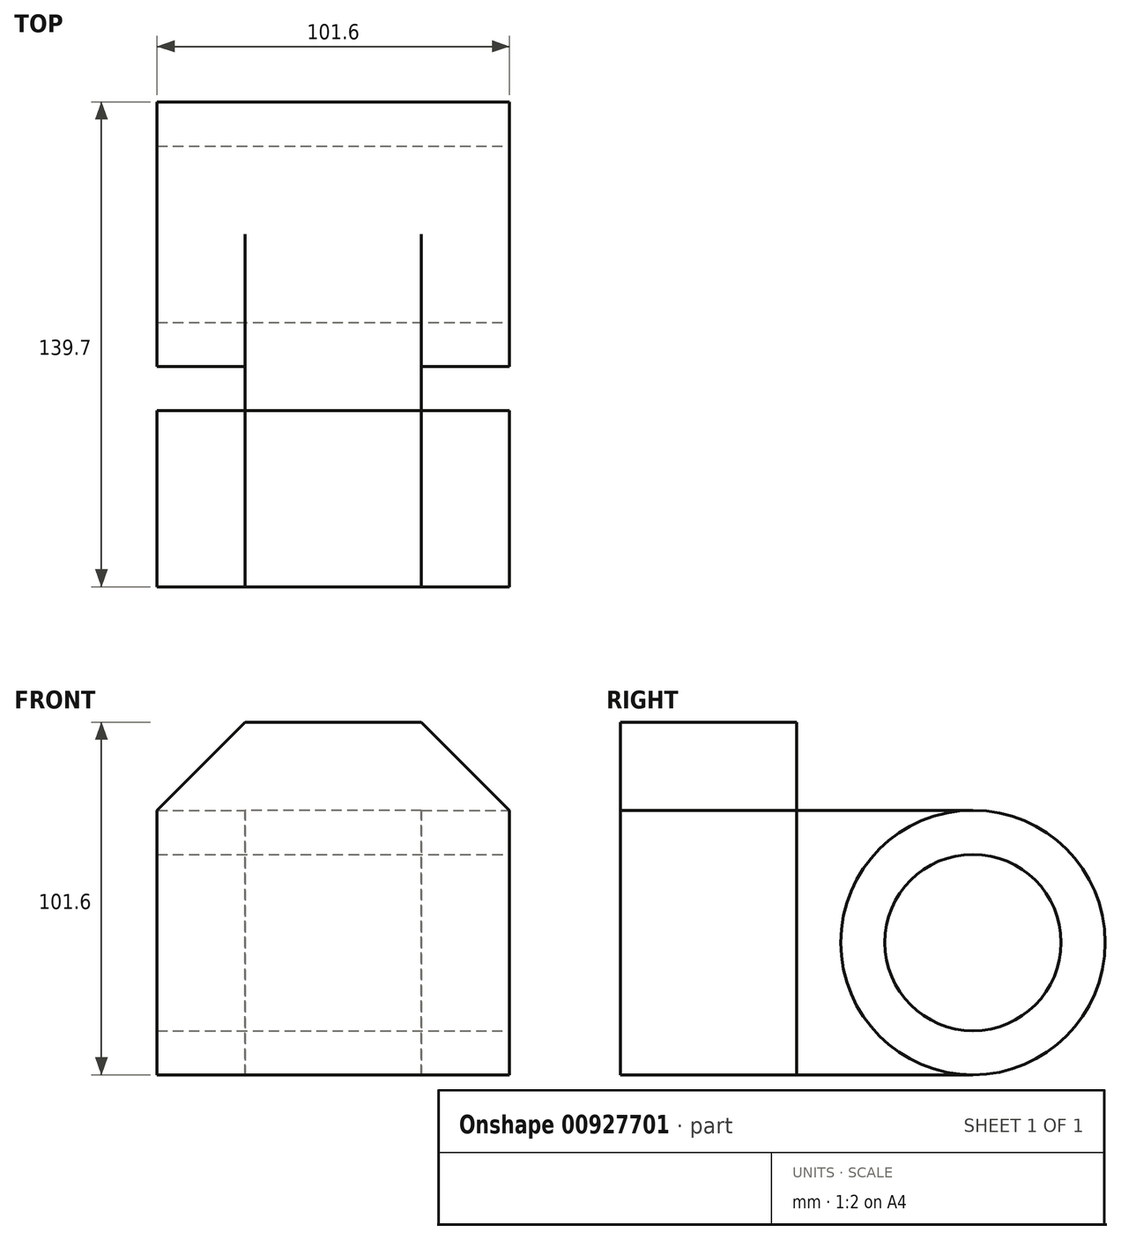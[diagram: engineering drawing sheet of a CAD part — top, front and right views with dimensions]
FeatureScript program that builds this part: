
annotation { "Feature Type Name" : "Feature", "Feature Type Description" : "" }
export const myFeature = defineFeature(function(context is Context, id is Id, definition is map)
    precondition{}
    {
        {
            var Q0;
            Q0=qCreatedBy(makeId("Top.planeOp"),FACE);
            var sketch = newSketch(context, id + "F0", { "sketchPlane" : qUnion([Q0])});
            skLineSegment(sketch, "E0.bottom", {"start": v(0, 0) * mm, "end": v(-101.6, 0) * mm});
            skLineSegment(sketch, "E0.top", {"start": v(0, 50.8) * mm, "end": v(-101.6, 50.8) * mm});
            skLineSegment(sketch, "E0.left", {"start": v(0, 0) * mm, "end": v(0, 50.8) * mm});
            skLineSegment(sketch, "E0.right", {"start": v(-101.6, 0) * mm, "end": v(-101.6, 50.8) * mm});
            skSolve(sketch);
        }
        {
            var Q0;
            Q0 = qSketchRegion(id + "F0", true);
            extrude(context, id + "F1", {"entities" : qUnion([Q0]), "depth" : 101.6 * mm, "offsetDistance" : 25.4 * mm});
        }
        {
            var Q0;
            Q0=makeQuery(id+"F1.opExtrude","SWEPT_FACE",FACE,{"disambiguationData":[OSD([sQuery(id+"F0.wireOp",EDGE,"E0.top")])]});
            var sketch = newSketch(context, id + "F2", { "sketchPlane" : qUnion([Q0])});
            skLineSegment(sketch, "E1", {"start": v(25.4, 101.6) * mm, "end": v(0, 76.2) * mm});
            skLineSegment(sketch, "E2", {"start": v(76.2, 101.6) * mm, "end": v(101.6, 76.2) * mm});
            skSolve(sketch);
        }
        {
            var Q0;
            {var subQ0=sQuery(id+"F2.wireOp",EDGE,"E1");Q0=makeQuery(id+"F2.imprint","IMPRINT",FACE,{"disambiguationData":[TD([[makeQuery(id+"F2.imprint","IMPRINT",EDGE,{"derivedFrom":subQ0}),-1.0]])]});}
            var Q1;
            {var subQ0=sQuery(id+"F2.wireOp",EDGE,"E2");Q1=makeQuery(id+"F2.imprint","IMPRINT",FACE,{"disambiguationData":[TD([[makeQuery(id+"F2.imprint","IMPRINT",EDGE,{"derivedFrom":subQ0}),1.0]])]});}
            extrude(context, id + "F3", {"entities" : qUnion([Q0, Q1]), "operationType" : NewBodyOperationType.REMOVE, "endBound" : BoundingType.THROUGH_ALL, "oppositeDirection" : true, "depth" : 25.4 * mm, "offsetDistance" : 25.4 * mm});
        }
        {
            var Q0;
            Q0=makeQuery(id+"F1.opExtrude","SWEPT_FACE",FACE,{"disambiguationData":[OSD([sQuery(id+"F0.wireOp",EDGE,"E0.top")])]});
            var sketch = newSketch(context, id + "F4", { "sketchPlane" : qUnion([Q0])});
            skLineSegment(sketch, "E3.bottom", {"start": v(25.4, 76.2) * mm, "end": v(76.2, 76.2) * mm});
            skLineSegment(sketch, "E3.top", {"start": v(25.4, 0) * mm, "end": v(76.2, 0) * mm});
            skLineSegment(sketch, "E3.left", {"start": v(25.4, 76.2) * mm, "end": v(25.4, 0) * mm});
            skLineSegment(sketch, "E3.right", {"start": v(76.2, 76.2) * mm, "end": v(76.2, 0) * mm});
            skSolve(sketch);
        }
        {
            var Q0;
            Q0 = qSketchRegion(id + "F4", true);
            extrude(context, id + "F5", {"entities" : qUnion([Q0]), "operationType" : NewBodyOperationType.ADD, "depth" : 50.8 * mm, "offsetDistance" : 25.4 * mm});
        }
        {
            var Q0;
            Q0=makeQuery(id+"F5.opExtrude","SWEPT_FACE",FACE,{"disambiguationData":[OSD([sQuery(id+"F4.wireOp",EDGE,"E3.right")])]});
            var sketch = newSketch(context, id + "F6", { "sketchPlane" : qUnion([Q0])});
            skCircle(sketch, "E4", {"center": v(-101.6, 38.1) * mm, "radius": 38.1 * mm});
            skCircle(sketch, "E5", {"center": v(-101.6, 38.1) * mm, "radius": 25.4 * mm});
            skSolve(sketch);
        }
        {
            var Q0;
            Q0 = qSketchRegion(id + "F6", true);
            var Q1;
            Q1=makeQuery(id+"F1.opExtrude","SWEPT_FACE",FACE,{"disambiguationData":[OSD([sQuery(id+"F0.wireOp",EDGE,"E0.right")])]});
            var Q2;
            Q2=makeQuery(id+"F1.opExtrude","SWEPT_FACE",FACE,{"disambiguationData":[OSD([sQuery(id+"F0.wireOp",EDGE,"E0.left")])]});
            extrude(context, id + "F7", {"entities" : qUnion([Q0]), "operationType" : NewBodyOperationType.ADD, "endBound" : BoundingType.UP_TO_SURFACE, "depth" : 25.4 * mm, "endBoundEntityFace" : qUnion([Q1]), "offsetDistance" : 25.4 * mm, "hasSecondDirection" : true, "secondDirectionBound" : SecondDirectionBoundingType.UP_TO_SURFACE, "secondDirectionOppositeDirection" : true, "secondDirectionDepth" : 25.4 * mm, "secondDirectionBoundEntityFace" : qUnion([Q2])});
        }
        {
            var Q0;
            {var subQ0=sQuery(id+"F4.wireOp",EDGE,"E3.right");Q0=makeQuery(id+"F7.boolean.opBoolean","SPLIT",FACE,{"disambiguationData":[TD([makeQuery(id+"F7.opExtrude","SWEPT_FACE",FACE,{"disambiguationData":[OSD([sQuery(id+"F6.wireOp",EDGE,"E5")])]})])],"derivedFrom":makeQuery(id+"F5.opExtrude","SWEPT_FACE",FACE,{"disambiguationData":[OSD([subQ0])]})});}
            extrude(context, id + "F8", {"entities" : qUnion([Q0]), "operationType" : NewBodyOperationType.REMOVE, "endBound" : BoundingType.THROUGH_ALL, "oppositeDirection" : true, "depth" : 25.4 * mm, "offsetDistance" : 25.4 * mm});
        }
    });
